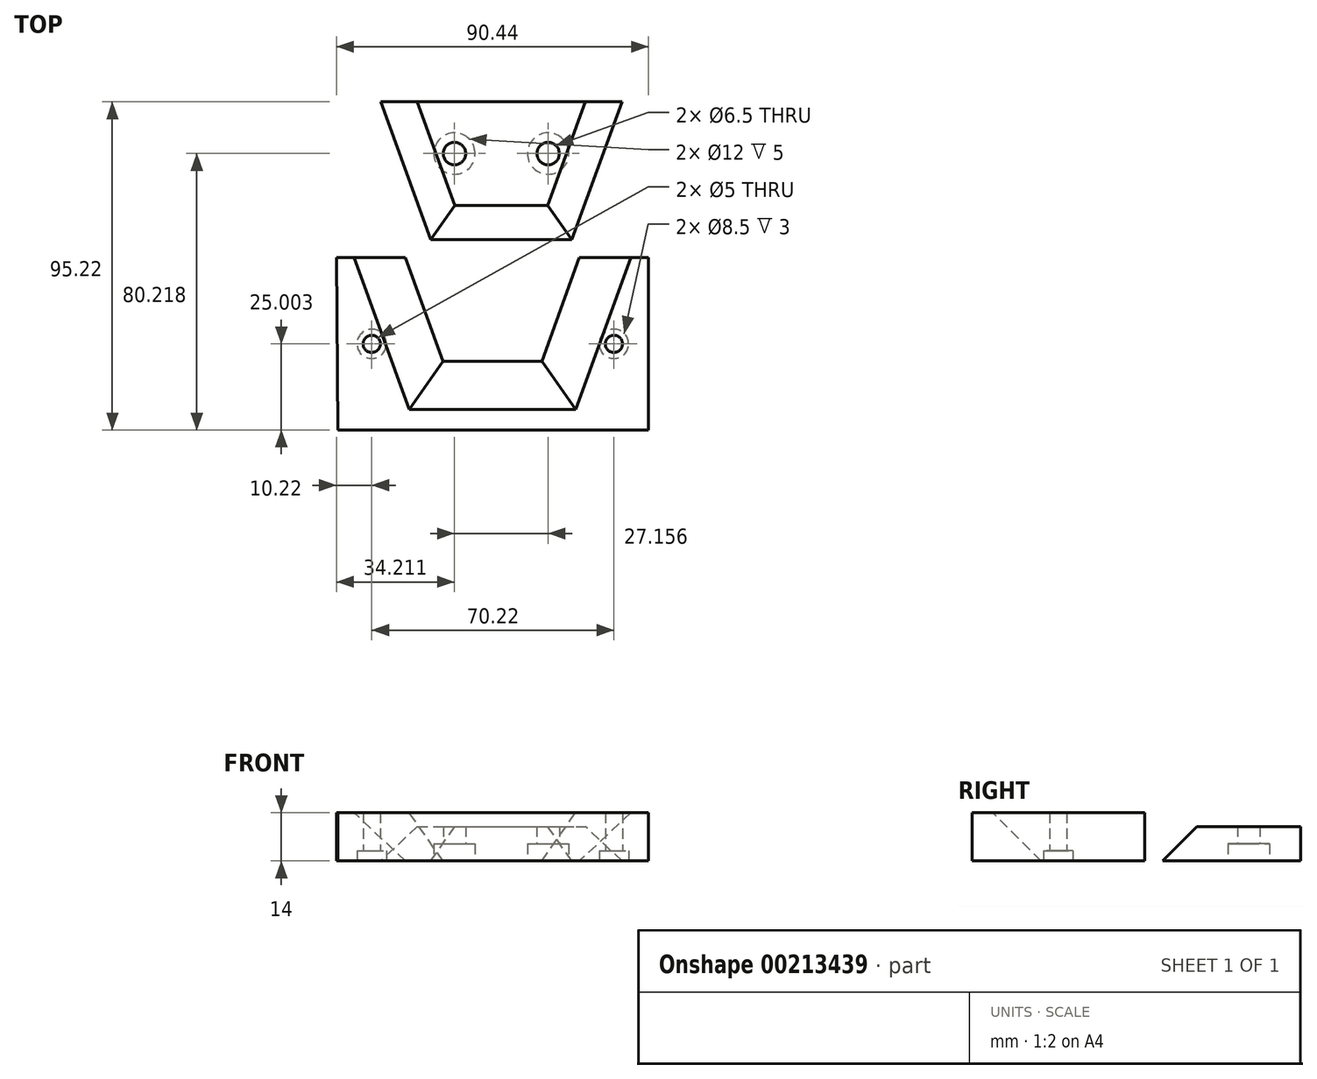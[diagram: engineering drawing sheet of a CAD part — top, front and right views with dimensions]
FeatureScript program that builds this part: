
annotation { "Feature Type Name" : "Feature", "Feature Type Description" : "" }
export const myFeature = defineFeature(function(context is Context, id is Id, definition is map)
    precondition{}
    {
        {
            var Q0;
            Q0=qCreatedBy(makeId("Top.planeOp"),FACE);
            var sketch = newSketch(context, id + "F0", { "sketchPlane" : qUnion([Q0])});
            skLineSegment(sketch, "E0", {"start": v(-39.06, 23.75) * mm, "end": v(-19.06, 23.75) * mm});
            skLineSegment(sketch, "E1", {"start": v(-19.06, 23.75) * mm, "end": v(-8.14, -6.25) * mm});
            skLineSegment(sketch, "E2", {"start": v(-8.14, -6.25) * mm, "end": v(20.46, -6.25) * mm});
            skLineSegment(sketch, "E3", {"start": v(20.46, -6.25) * mm, "end": v(31.38, 23.75) * mm});
            skLineSegment(sketch, "E4", {"start": v(31.38, 23.75) * mm, "end": v(51.38, 23.75) * mm});
            skLineSegment(sketch, "E5", {"start": v(51.38, 23.75) * mm, "end": v(51.38, -26.25) * mm});
            skLineSegment(sketch, "E6", {"start": v(51.38, -26.25) * mm, "end": v(-38.62, -26.25) * mm});
            skLineSegment(sketch, "E7", {"start": v(-38.62, -26.25) * mm, "end": v(-39.06, 23.75) * mm});
            skCircle(sketch, "E8", {"center": v(-28.84, -1.25) * mm, "radius": 2.5 * mm});
            skCircle(sketch, "E9", {"center": v(41.38, -1.25) * mm, "radius": 2.5 * mm});
            skSolve(sketch);
        }
        {
            var Q0;
            Q0=makeQuery(id+"F0.imprint","IMPRINT",FACE,{"disambiguationData":[TD([[makeQuery(id+"F0.imprint","IMPRINT",EDGE,{"derivedFrom":sQuery(id+"F0.wireOp",EDGE,"E0")}),-1.0]])]});
            extrude(context, id + "F1", {"entities" : qUnion([Q0]), "depth" : 14 * mm});
        }
        {
            var Q0;
            Q0=makeQuery(id+"F1.opExtrude","CAP_EDGE",EDGE,{"disambiguationData":[OSD([sQuery(id+"F0.wireOp",EDGE,"E1")])],"isStart":false});
            var Q1;
            Q1=makeQuery(id+"F1.opExtrude","CAP_EDGE",EDGE,{"disambiguationData":[OSD([sQuery(id+"F0.wireOp",EDGE,"E2")])],"isStart":false});
            var Q2;
            Q2=makeQuery(id+"F1.opExtrude","CAP_EDGE",EDGE,{"disambiguationData":[OSD([sQuery(id+"F0.wireOp",EDGE,"E3")])],"isStart":false});
            chamfer(context, id + "F2", {"entities" : qUnion([Q0, Q1, Q2]), "width" : 14 * mm, "tangentPropagation" : true});
        }
        {
            var Q0;
            Q0=qCreatedBy(makeId("Top.planeOp"),FACE);
            var sketch = newSketch(context, id + "F3", { "sketchPlane" : qUnion([Q0])});
            skLineSegment(sketch, "E10", {"start": v(-26.27, 68.97) * mm, "end": v(43.73, 68.97) * mm});
            skLineSegment(sketch, "E11", {"start": v(43.73, 68.97) * mm, "end": v(29.17, 28.97) * mm});
            skLineSegment(sketch, "E12", {"start": v(29.17, 28.97) * mm, "end": v(-11.71, 28.97) * mm});
            skLineSegment(sketch, "E13", {"start": v(-11.71, 28.97) * mm, "end": v(-26.27, 68.97) * mm});
            skCircle(sketch, "E14", {"center": v(-4.85, 53.97) * mm, "radius": 3.25 * mm});
            skCircle(sketch, "E15", {"center": v(22.3, 53.97) * mm, "radius": 3.25 * mm});
            skSolve(sketch);
        }
        {
            var Q0;
            Q0=makeQuery(id+"F3.imprint","IMPRINT",FACE,{"disambiguationData":[TD([[makeQuery(id+"F3.imprint","IMPRINT",EDGE,{"derivedFrom":sQuery(id+"F3.wireOp",EDGE,"E10")}),-1.0]])]});
            extrude(context, id + "F4", {"entities" : qUnion([Q0]), "depth" : 10 * mm});
        }
        {
            var Q0;
            Q0=makeQuery(id+"F4.opExtrude","CAP_EDGE",EDGE,{"disambiguationData":[OSD([sQuery(id+"F3.wireOp",EDGE,"E12")])],"isStart":false});
            var Q1;
            Q1=makeQuery(id+"F4.opExtrude","CAP_EDGE",EDGE,{"disambiguationData":[OSD([sQuery(id+"F3.wireOp",EDGE,"E13")])],"isStart":false});
            var Q2;
            Q2=makeQuery(id+"F4.opExtrude","CAP_EDGE",EDGE,{"disambiguationData":[OSD([sQuery(id+"F3.wireOp",EDGE,"E11")])],"isStart":false});
            chamfer(context, id + "F5", {"entities" : qUnion([Q0, Q1, Q2]), "width" : 10 * mm, "tangentPropagation" : true});
        }
        {
            var Q0;
            Q0=sQuery(id+"F3.wireOp",VERTEX,"E14.center");
            var Q1;
            Q1=makeQuery(id+"F4.opExtrude","SWEPT_BODY",BODY,{"disambiguationData":[OSD([sQuery(id+"F3.wireOp",EDGE,"E10"),sQuery(id+"F3.wireOp",EDGE,"E11"),sQuery(id+"F3.wireOp",EDGE,"E12"),sQuery(id+"F3.wireOp",EDGE,"E13"),sQuery(id+"F3.wireOp",EDGE,"E14"),sQuery(id+"F3.wireOp",EDGE,"E15")])]});
            hole(context, id + "F6", {"style" : HoleStyle.C_BORE, "endStyle" : HoleEndStyle.THROUGH, "oppositeDirection" : true, "holeDiameter" : 6.5 * mm, "cBoreDiameter" : 12 * mm, "cBoreDepth" : 5 * mm, "startFromSketch" : true, "locations" : qUnion([Q0]), "scope" : qUnion([Q1]), "isTappedThrough" : true});
        }
        {
            var Q0;
            Q0=sQuery(id+"F3.wireOp",VERTEX,"E15.center");
            var Q1;
            Q1=makeQuery(id+"F4.opExtrude","SWEPT_BODY",BODY,{"disambiguationData":[OSD([sQuery(id+"F3.wireOp",EDGE,"E10"),sQuery(id+"F3.wireOp",EDGE,"E11"),sQuery(id+"F3.wireOp",EDGE,"E12"),sQuery(id+"F3.wireOp",EDGE,"E13"),sQuery(id+"F3.wireOp",EDGE,"E14"),sQuery(id+"F3.wireOp",EDGE,"E15")])]});
            hole(context, id + "F7", {"style" : HoleStyle.C_BORE, "endStyle" : HoleEndStyle.THROUGH, "oppositeDirection" : true, "holeDiameter" : 6.5 * mm, "cBoreDiameter" : 12 * mm, "cBoreDepth" : 5 * mm, "startFromSketch" : true, "locations" : qUnion([Q0]), "scope" : qUnion([Q1]), "isTappedThrough" : true});
        }
        {
            var Q0;
            Q0=sQuery(id+"F0.wireOp",VERTEX,"E8.center");
            var Q1;
            Q1=makeQuery(id+"F1.opExtrude","SWEPT_BODY",BODY,{"disambiguationData":[OSD([sQuery(id+"F0.wireOp",EDGE,"E0"),sQuery(id+"F0.wireOp",EDGE,"E1"),sQuery(id+"F0.wireOp",EDGE,"E2"),sQuery(id+"F0.wireOp",EDGE,"E3"),sQuery(id+"F0.wireOp",EDGE,"E4"),sQuery(id+"F0.wireOp",EDGE,"E5"),sQuery(id+"F0.wireOp",EDGE,"E6"),sQuery(id+"F0.wireOp",EDGE,"E7"),sQuery(id+"F0.wireOp",EDGE,"E8"),sQuery(id+"F0.wireOp",EDGE,"E9")])]});
            hole(context, id + "F8", {"style" : HoleStyle.C_BORE, "endStyle" : HoleEndStyle.THROUGH, "oppositeDirection" : true, "holeDiameter" : 5 * mm, "cBoreDiameter" : 8.5 * mm, "cBoreDepth" : 3 * mm, "locations" : qUnion([Q0]), "scope" : qUnion([Q1]), "isTappedThrough" : true});
        }
        {
            var Q0;
            Q0=sQuery(id+"F0.wireOp",VERTEX,"E9.center");
            var Q1;
            Q1=makeQuery(id+"F1.opExtrude","SWEPT_BODY",BODY,{"disambiguationData":[OSD([sQuery(id+"F0.wireOp",EDGE,"E0"),sQuery(id+"F0.wireOp",EDGE,"E1"),sQuery(id+"F0.wireOp",EDGE,"E2"),sQuery(id+"F0.wireOp",EDGE,"E3"),sQuery(id+"F0.wireOp",EDGE,"E4"),sQuery(id+"F0.wireOp",EDGE,"E5"),sQuery(id+"F0.wireOp",EDGE,"E6"),sQuery(id+"F0.wireOp",EDGE,"E7"),sQuery(id+"F0.wireOp",EDGE,"E8"),sQuery(id+"F0.wireOp",EDGE,"E9")])]});
            hole(context, id + "F9", {"style" : HoleStyle.C_BORE, "endStyle" : HoleEndStyle.THROUGH, "oppositeDirection" : true, "holeDiameter" : 5 * mm, "cBoreDiameter" : 8.5 * mm, "cBoreDepth" : 3 * mm, "locations" : qUnion([Q0]), "scope" : qUnion([Q1]), "isTappedThrough" : true});
        }
    });
